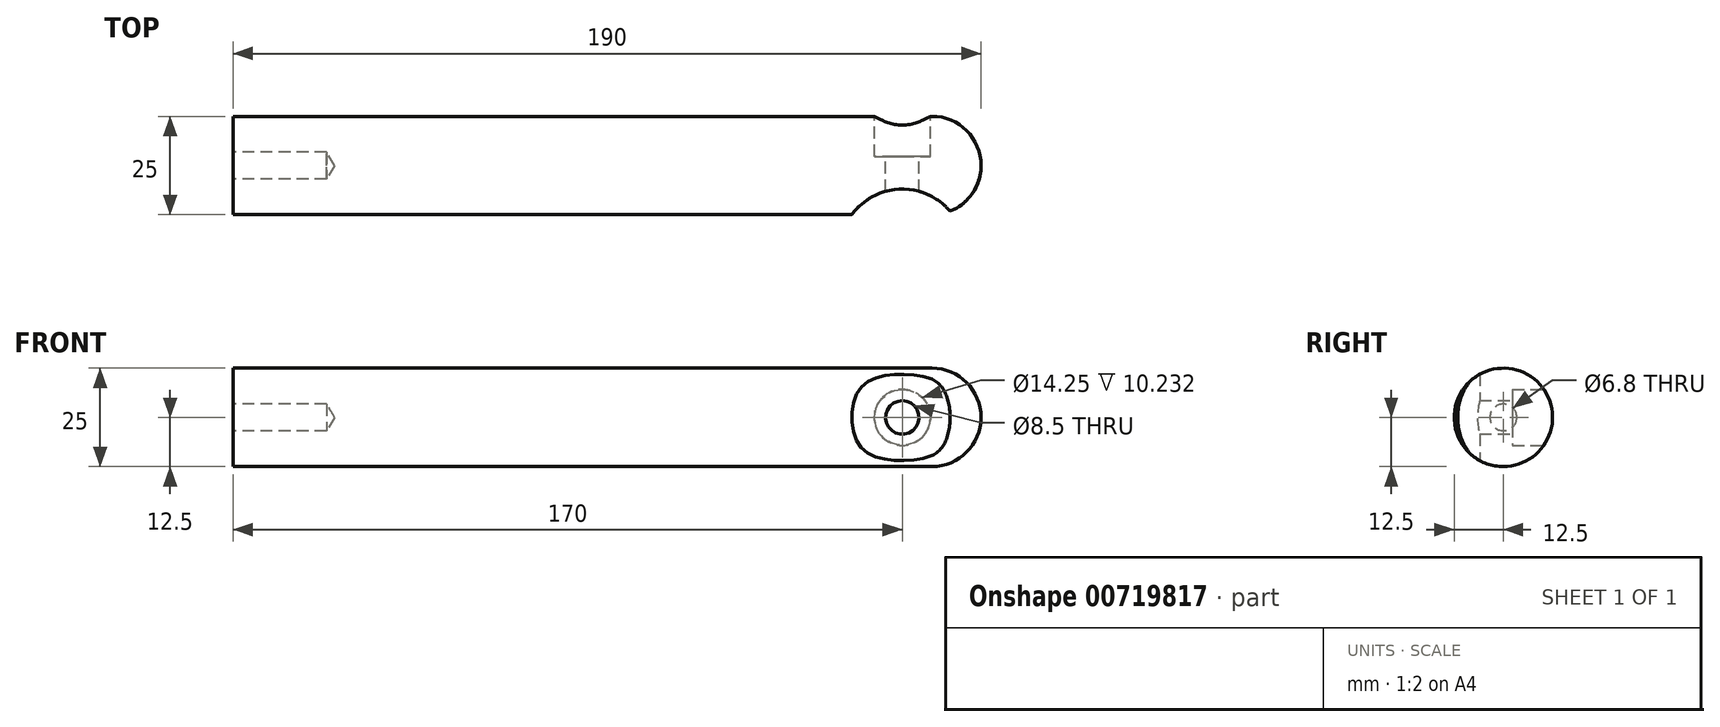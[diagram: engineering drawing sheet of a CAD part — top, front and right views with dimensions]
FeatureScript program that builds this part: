
annotation { "Feature Type Name" : "Feature", "Feature Type Description" : "" }
export const myFeature = defineFeature(function(context is Context, id is Id, definition is map)
    precondition{}
    {
        {
            var Q0;
            Q0=qCreatedBy(makeId("Top.planeOp"),FACE);
            var sketch = newSketch(context, id + "F0", { "sketchPlane" : qUnion([Q0])});
            skLineSegment(sketch, "E0.bottom", {"start": v(0, 0) * mm, "end": v(190, 0) * mm});
            skLineSegment(sketch, "E0.top", {"start": v(0, 12.5) * mm, "end": v(177.5, 12.5) * mm});
            skLineSegment(sketch, "E0.left", {"start": v(0, 0) * mm, "end": v(0, 12.5) * mm});
            skLineSegment(sketch, "E0.right", {"start": v(190, 0) * mm, "end": v(190, 0) * mm});
            skPoint(sketch, "E1.visualSharp", {"position": v(190, 12.5) * mm});
            skArc(sketch, "E1.filletArc", {"start": v(190, 0) * mm, "mid": v(186.34, 8.84) * mm, "end": v(177.5, 12.5) * mm});
            skSolve(sketch);
        }
        {
            var Q0;
            Q0=qCreatedBy(makeId("Top.planeOp"),FACE);
            var sketch = newSketch(context, id + "F1", { "sketchPlane" : qUnion([Q0])});
            skLineSegment(sketch, "E2", {"start": v(64.67, 0) * mm, "end": v(-52.07, 0) * mm, "construction": true});
            skSolve(sketch);
        }
        {
            var Q0;
            Q0=makeQuery(id+"F0.imprint","IMPRINT",FACE,{"disambiguationData":[TD([[makeQuery(id+"F0.imprint","IMPRINT",EDGE,{"derivedFrom":sQuery(id+"F0.wireOp",EDGE,"E0.bottom")}),1.0]])]});
            var Q1;
            Q1=sQuery(id+"F1.wireOp",EDGE,"E2");
            var Q2;
            Q2=sQuery(id+"F0.wireOp",EDGE,"E0.top");
            var Q3;
            Q3=sQuery(id+"F0.wireOp",EDGE,"E0.left");
            var Q4;
            Q4=sQuery(id+"F0.wireOp",EDGE,"E0.bottom");
            var Q5;
            Q5=sQuery(id+"F0.wireOp",EDGE,"E1.filletArc");
            var Q6;
            Q6=sQuery(id+"F1.wireOp",EDGE,"E2");
            revolve(context, id + "F2", {"surfaceOperationType" : NewSurfaceOperationType.NEW, "entities" : qUnion([Q0]), "surfaceEntities" : qUnion([Q1, Q2, Q3, Q4, Q5]), "axis" : qUnion([Q6]), "revolveType" : RevolveType.FULL});
        }
        {
            var Q0;
            Q0=qCreatedBy(makeId("Top.planeOp"),FACE);
            var sketch = newSketch(context, id + "F3", { "sketchPlane" : qUnion([Q0])});
            skCircle(sketch, "E3", {"center": v(170, -22) * mm, "radius": 16 * mm});
            skSolve(sketch);
        }
        {
            var Q0;
            Q0 = qSketchRegion(id + "F3", true);
            extrude(context, id + "F4", {"entities" : qUnion([Q0]), "operationType" : NewBodyOperationType.REMOVE, "endBound" : BoundingType.SYMMETRIC, "depth" : 30 * mm, "offsetDistance" : 25 * mm});
        }
        {
            var Q0;
            Q0=qCreatedBy(makeId("Right.planeOp"),FACE);
            var sketch = newSketch(context, id + "F5", { "sketchPlane" : qUnion([Q0])});
            skPoint(sketch, "E4", {"position": v(0, 0) * mm});
            skSolve(sketch);
        }
        {
            var Q0;
            Q0=sQuery(id+"F5.wireOp",VERTEX,"E4");
            var Q1;
            Q1=makeQuery(id+"F2.opRevolve","SWEPT_BODY",BODY,{"disambiguationData":[OSD([sQuery(id+"F0.wireOp",EDGE,"E0.bottom"),sQuery(id+"F0.wireOp",EDGE,"E0.top"),sQuery(id+"F0.wireOp",EDGE,"E0.left"),sQuery(id+"F0.wireOp",EDGE,"E1.filletArc")])]});
            hole(context, id + "F6", {"style" : HoleStyle.SIMPLE, "endStyle" : HoleEndStyle.BLIND, "oppositeDirection" : true, "standardTappedOrClearance" : lookupTablePath({ "standard" : "ISO", "engagement" : "75%", "pitch" : "1.25 mm", "size" : "M8", "type" : "Tapped" }), "standardBlindInLast" : lookupTablePath({ "standard" : "ISO", "engagement" : "75%", "pitch" : "1.25 mm", "size" : "M8", "type" : "Tapped" }), "holeDiameter" : 6.8 * mm, "majorDiameter" : 8 * mm, "showTappedDepth" : true, "holeDepth" : 23.75 * mm, "isTappedThrough" : true, "tappedDepth" : 20 * mm, "tapClearance" : 3, "startFromSketch" : true, "locations" : qUnion([Q0]), "scope" : qUnion([Q1])});
        }
        {
            var Q0;
            Q0=qCreatedBy(makeId("Front.planeOp"),FACE);
            cPlane(context, id + "F7", {"entities" : qUnion([Q0]), "cplaneType" : CPlaneType.OFFSET, "offset" : 12.5 * mm, "oppositeDirection" : true, "width" : 150 * mm, "height" : 150 * mm});
        }
        {
            var Q0;
            Q0=qCreatedBy(id+"F7.planeOp",FACE);
            var sketch = newSketch(context, id + "F8", { "sketchPlane" : qUnion([Q0])});
            skPoint(sketch, "E5", {"position": v(170, 0) * mm});
            skSolve(sketch);
        }
        {
            var Q0;
            Q0=sQuery(id+"F8.wireOp",VERTEX,"E5");
            var Q1;
            Q1=makeQuery(id+"F2.opRevolve","SWEPT_BODY",BODY,{"disambiguationData":[OSD([sQuery(id+"F0.wireOp",EDGE,"E0.bottom"),sQuery(id+"F0.wireOp",EDGE,"E0.top"),sQuery(id+"F0.wireOp",EDGE,"E0.left"),sQuery(id+"F0.wireOp",EDGE,"E1.filletArc")])]});
            hole(context, id + "F9", {"style" : HoleStyle.C_BORE, "endStyle" : HoleEndStyle.THROUGH, "oppositeDirection" : true, "holeDiameter" : 8.5 * mm, "cBoreDiameter" : 14.25 * mm, "cBoreDepth" : 8 * mm, "majorDiameter" : 8 * mm, "isTappedThrough" : true, "tappedDepth" : 20 * mm, "tapClearance" : 3, "locations" : qUnion([Q0]), "scope" : qUnion([Q1])});
        }
    });
